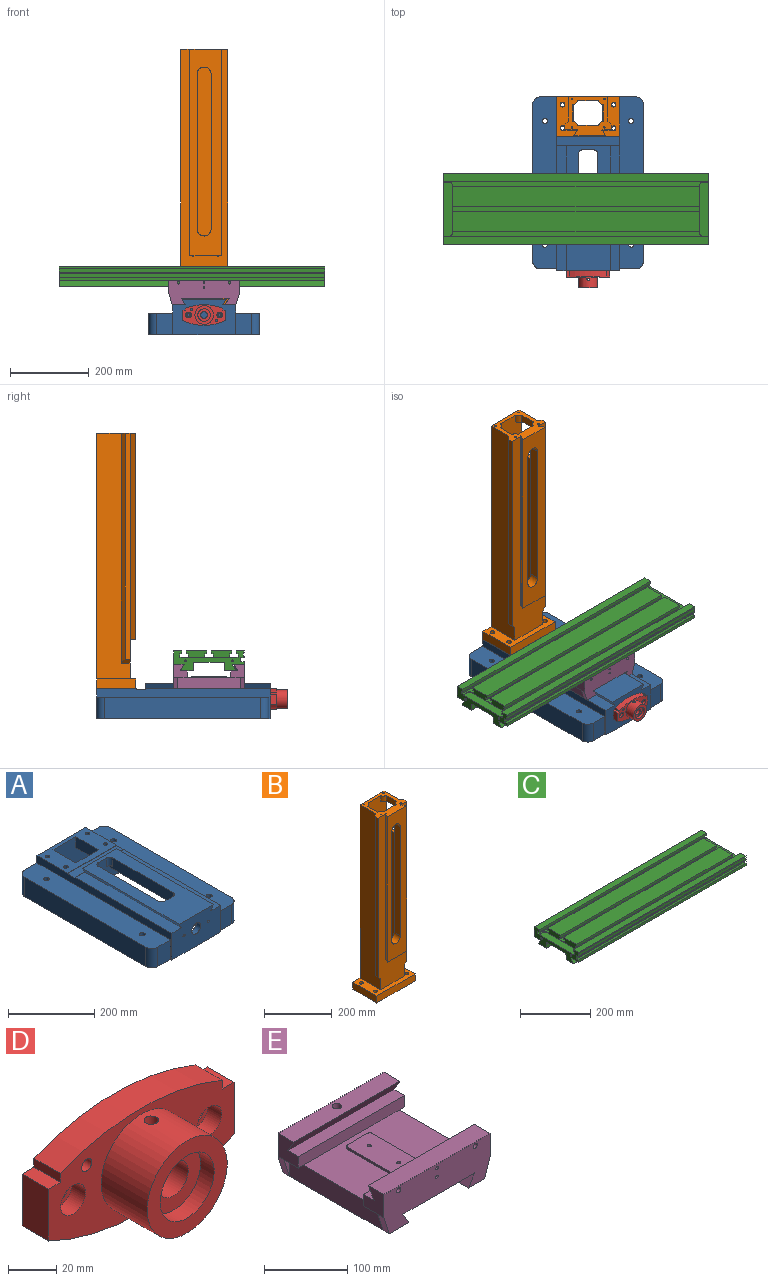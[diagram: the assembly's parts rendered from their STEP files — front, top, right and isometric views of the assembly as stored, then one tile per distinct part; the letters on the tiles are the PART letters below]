
ASSEMBLY  parts=5 mates=4
PART A: 110 faces, bbox 282x443x90 mm
  f0: plane 83x51mm, normal (0,0,-1), area 4078.8mm2, adj f11,f45,f46,f62,f81,f106
  f1: plane 100x36mm, normal (0,0,-1), area 3600mm2, adj f2,f77,f91,f102
  f2: plane 293x26mm, normal (-1,0,0), area 7222.3mm2, adj f1,f7,f10,f11,f13,f82,f89,f90
  f3: plane 83x36mm, normal (0,0,-1), area 2988mm2, adj f4,f11,f75,f100
  f4: plane 293x26mm, normal (1,0,0), area 7222.3mm2, adj f3,f8,f10,f11,f70,f80,f86,f87
  f5: plane 100x51mm, normal (0,0,-1), area 5100mm2, adj f50,f79,f85,f96
  f6: plane 100x51mm, normal (0,0,-1), area 5100mm2, adj f46,f81,f94,f105
  f7: plane 90x36mm, normal (0,0,-1), area 3240mm2, adj f2,f10,f77,f90
  f8: plane 100x36mm, normal (0,0,-1), area 3600mm2, adj f4,f75,f88,f99
  f9: plane 90x51mm, normal (0,0,-1), area 4590mm2, adj f10,f50,f79,f84
  f10: plane 262x90mm, normal (0,-1,0), area 9651.3mm2, adj f2,f4,f7,f9,f15,f16,f19,f20
  f11: plane 242x65mm, normal (0,1,0), area 12693.9mm2, adj f0,f2,f3,f4,f12,f13,f14,f21
  f12: plane 83x51mm, normal (0,0,-1), area 4078.8mm2, adj f11,f50,f51,f67,f79,f97
  f13: plane 83x36mm, normal (0,0,-1), area 2988mm2, adj f2,f11,f77,f103
  f14: plane 84x48mm, normal (0,0,-1), area 3594.9mm2, adj f11,f21,f22,f23,f24,f25
  f15: plane 10x10mm, normal (0,0,-1), area 21.5mm2, adj f10,f19,f25
  f16: plane 10x10mm, normal (0,0,-1), area 21.5mm2, adj f10,f20,f21
  f17: plane 108x93.5mm, normal (0,0,-1), area 9780.4mm2, adj f27,f28,f47,f48,f63,f64,f68,f73
  f18: plane 108x93.5mm, normal (0,0,-1), area 9780.4mm2, adj f27,f29,f48,f49,f61,f65,f66,f72
  f19: cylinder r=10mm len=25mm, axis (0,0,1), area 392.7mm2, adj f10,f15,f25,f55
  f20: cylinder r=10mm len=25mm, axis (0,0,1), area 392.7mm2, adj f10,f16,f21,f55
  f21: plane 293x31mm, normal (1,0,0), area 6733mm2, adj f10,f11,f14,f16,f20,f22,f55,f76
  f22: cylinder r=10mm len=25mm, axis (0,0,1), area 392.7mm2, adj f14,f21,f23,f55
  f23: plane 28x25mm, normal (0,1,0), area 700mm2, adj f14,f22,f24,f55
  f24: cylinder r=10mm len=25mm, axis (0,0,1), area 392.7mm2, adj f14,f23,f25,f55
  f25: plane 293x31mm, normal (-1,0,0), area 6733mm2, adj f10,f11,f14,f15,f19,f24,f55,f78
  f26: plane 443x282mm, normal (0,0,-1), area 14950.5mm2, adj f10,f11,f27,f28,f29,f33,f34,f36
  f27: plane 262x62mm, normal (0,1,0), area 7666.3mm2, adj f17,f18,f26,f28,f29,f69,f72,f73
  f28: plane 98x45mm, normal (-1,0,0), area 4410mm2, adj f17,f26,f27,f47
  f29: plane 98x45mm, normal (1,0,0), area 4410mm2, adj f18,f26,f27,f49
  f30: plane 160x101mm, normal (0,0,1), area 10208.1mm2, adj f33,f40,f48,f52,f59,f61,f64,f65
  f31: plane 90x51mm, normal (0,0,-1), area 4590mm2, adj f10,f46,f81,f93
  f32: plane 318x32.08mm, normal (0,0,1), area 10202.4mm2, adj f33,f54,f57,f58
  f33: plane 443x76mm, normal (-1,0,0), area 9554mm2, adj f26,f30,f32,f36,f40,f44,f57,f58
  f34: plane 55x41mm, normal (0,-1,0), area 2255mm2, adj f26,f35,f37,f52
  f35: plane 438x61mm, normal (0,0,1), area 26280.9mm2, adj f34,f37,f38,f39,f40,f52,f62,f63
  f36: plane 55x41mm, normal (0,-1,0), area 2255mm2, adj f26,f33,f43,f44
  f37: cylinder r=20mm len=55mm, axis (0,0,1), area 1727.9mm2, adj f26,f34,f35,f38
  f38: plane 398x55mm, normal (1,0,0), area 21890mm2, adj f26,f35,f37,f39
  f39: cylinder r=20mm len=55mm, axis (0,0,1), area 1727.9mm2, adj f26,f35,f38,f40
  f40: plane 242x76mm, normal (0,1,0), area 16670mm2, adj f26,f30,f33,f35,f39,f41,f44,f52
  f41: cylinder r=20mm len=55mm, axis (0,0,1), area 1727.9mm2, adj f26,f40,f42,f44
  f42: plane 398x55mm, normal (-1,0,0), area 21890mm2, adj f26,f41,f43,f44
  f43: cylinder r=20mm len=55mm, axis (0,0,1), area 1727.9mm2, adj f26,f36,f42,f44
  f44: plane 438x61mm, normal (0,0,1), area 26280.9mm2, adj f33,f36,f40,f41,f42,f43,f66,f67
  f45: cylinder r=10mm len=45mm, axis (0,0,1), area 706.9mm2, adj f0,f11,f26,f46
  f46: plane 283x45mm, normal (-1,0,0), area 12184.1mm2, adj f0,f6,f10,f26,f31,f45,f92,f93
  f47: cylinder r=10mm len=45mm, axis (0,0,1), area 706.9mm2, adj f17,f26,f28,f48
  f48: plane 242x76mm, normal (0,-1,0), area 13215mm2, adj f17,f18,f26,f30,f47,f49,f72,f73
  f49: cylinder r=10mm len=45mm, axis (0,0,1), area 706.9mm2, adj f18,f26,f29,f48
  f50: plane 283x45mm, normal (1,0,0), area 12184.1mm2, adj f5,f9,f10,f12,f26,f51,f83,f84
  f51: cylinder r=10mm len=45mm, axis (0,0,1), area 706.9mm2, adj f11,f12,f26,f50
  f52: plane 443x76mm, normal (1,0,0), area 9554mm2, adj f26,f30,f34,f35,f40,f53,f57,f58
  f53: plane 318x32.08mm, normal (0,0,1), area 10202.4mm2, adj f52,f56,f57,f58
  f54: plane 318x14mm, normal (-0.87,0,-0.5), area 5140.7mm2, adj f32,f55,f57,f58
  f55: plane 318x112mm, normal (0,0,1), area 25189.8mm2, adj f10,f19,f20,f21,f22,f23,f24,f25
  f56: plane 318x14mm, normal (0.87,0,-0.5), area 5140.7mm2, adj f53,f55,f57,f58
  f57: plane 160x90mm, normal (0,-1,0), area 12858.7mm2, adj f26,f32,f33,f52,f53,f54,f55,f56
  f58: plane 160x15mm, normal (0,1,0), area 1614.8mm2, adj f32,f33,f52,f53,f54,f55,f56,f60
  f59: plane 160x1mm, normal (0,-1,0), area 160mm2, adj f30,f33,f52,f60
  f60: plane 160x24mm, normal (0,0,1), area 3840mm2, adj f33,f52,f58,f59
  f61: cylinder r=5.1mm len=31mm, axis (0,0,1), area 993.4mm2, adj f18,f30
  f62: cylinder r=6.5mm len=13mm, axis (0,0,1), area 408.4mm2, adj f0,f35
  f63: cylinder r=6.5mm len=13mm, axis (0,0,1), area 408.4mm2, adj f17,f35
  f64: cylinder r=5.1mm len=31mm, axis (0,0,1), area 993.4mm2, adj f17,f30
  f65: cylinder r=5.1mm len=31mm, axis (0,0,1), area 993.4mm2, adj f18,f30
  f66: cylinder r=6.5mm len=13mm, axis (0,0,1), area 408.4mm2, adj f18,f44
  f67: cylinder r=6.5mm len=13mm, axis (0,0,1), area 408.4mm2, adj f12,f44
  f68: cylinder r=5.1mm len=31mm, axis (0,0,1), area 993.4mm2, adj f17,f30
  f69: cylinder r=228.11mm len=238mm, axis (0,1,0), area 4256.5mm2, adj f10,f26,f27
  f70: plane 90x36mm, normal (0,0,-1), area 3240mm2, adj f4,f10,f75,f87
  f71: plane 75x14mm, normal (0,1,0), area 1050mm2, adj f30,f72,f73,f74
  f72: plane 108x31mm, normal (1,0,0), area 2886mm2, adj f18,f27,f30,f48,f71,f74
  f73: plane 108x31mm, normal (-1,0,0), area 2886mm2, adj f17,f27,f30,f48,f71,f74
  f74: plane 75x33mm, normal (0,0,-1), area 2475mm2, adj f27,f71,f72,f73
  f75: plane 293x6mm, normal (-1,0,0), area 1698mm2, adj f3,f8,f10,f11,f70,f76,f86,f87
  f76: plane 293x10mm, normal (0,0,-1), area 2930mm2, adj f10,f11,f21,f75
  f77: plane 293x6mm, normal (1,0,0), area 1698mm2, adj f1,f7,f10,f11,f13,f78,f89,f90
  f78: plane 293x10mm, normal (0,0,-1), area 2930mm2, adj f10,f11,f25,f77
  f79: plane 293x6mm, normal (-1,0,0), area 1682.7mm2, adj f5,f9,f10,f11,f12,f80,f83,f84
  f80: plane 293x10mm, normal (0,0,-1), area 2930mm2, adj f4,f10,f11,f79
  f81: plane 293x6mm, normal (1,0,0), area 1682.7mm2, adj f0,f6,f10,f11,f31,f82,f92,f93
  f82: plane 293x10mm, normal (0,0,-1), area 2930mm2, adj f2,f10,f11,f81
  f83: plane 51x23.78mm, normal (0.42,0,-0.91), area 562.7mm2, adj f50,f79,f84,f85
  f84: plane 51x27.55mm, normal (0,1,0), area 798.5mm2, adj f9,f50,f79,f83
  f85: plane 51x27.55mm, normal (0,-1,0), area 798.5mm2, adj f5,f50,f79,f83
  f86: plane 36x16.79mm, normal (0.42,0,-0.91), area 397.2mm2, adj f4,f75,f87,f88
  f87: plane 36x19.79mm, normal (0,1,0), area 410.2mm2, adj f4,f70,f75,f86
  f88: plane 36x19.79mm, normal (0,-1,0), area 410.2mm2, adj f4,f8,f75,f86
  f89: plane 36x16.79mm, normal (-0.42,0,-0.91), area 397.2mm2, adj f2,f77,f90,f91
  f90: plane 36x19.79mm, normal (0,1,0), area 410.2mm2, adj f2,f7,f77,f89
  f91: plane 36x19.79mm, normal (0,-1,0), area 410.2mm2, adj f1,f2,f77,f89
  f92: plane 51x23.78mm, normal (-0.42,0,-0.91), area 562.7mm2, adj f46,f81,f93,f94
  f93: plane 51x27.55mm, normal (0,1,0), area 798.5mm2, adj f31,f46,f81,f92
  f94: plane 51x27.55mm, normal (0,-1,0), area 798.5mm2, adj f6,f46,f81,f92
  f95: plane 51x23.78mm, normal (0.42,0,-0.91), area 562.7mm2, adj f50,f79,f96,f97
  f96: plane 51x27.55mm, normal (0,1,0), area 798.5mm2, adj f5,f50,f79,f95
  f97: plane 51x27.55mm, normal (0,-1,0), area 798.5mm2, adj f12,f50,f79,f95
  f98: plane 36x16.79mm, normal (0.42,0,-0.91), area 397.2mm2, adj f4,f75,f99,f100
  f99: plane 36x19.79mm, normal (0,1,0), area 410.2mm2, adj f4,f8,f75,f98
  f100: plane 36x19.79mm, normal (0,-1,0), area 410.2mm2, adj f3,f4,f75,f98
  f101: plane 36x16.79mm, normal (-0.42,0,-0.91), area 397.2mm2, adj f2,f77,f102,f103
  f102: plane 36x19.79mm, normal (0,1,0), area 410.2mm2, adj f1,f2,f77,f101
  f103: plane 36x19.79mm, normal (0,-1,0), area 410.2mm2, adj f2,f13,f77,f101
  f104: plane 51x23.78mm, normal (-0.42,0,-0.91), area 562.7mm2, adj f46,f81,f105,f106
  f105: plane 51x27.55mm, normal (0,1,0), area 798.5mm2, adj f6,f46,f81,f104
  f106: plane 51x27.55mm, normal (0,-1,0), area 798.5mm2, adj f0,f46,f81,f104
  f107: cylinder r=14.75mm len=29.5mm, axis (0,1,0), area 1390.2mm2, adj f11,f57
  f108: cylinder r=3.4mm len=15mm, axis (0,-1,0), area 320.4mm2, adj f11,f57
  f109: cylinder r=3.4mm len=15mm, axis (0,-1,0), area 320.4mm2, adj f11,f57
PART B: 65 faces, bbox 160x100x650 mm
  f0: plane 625x120mm, normal (0,-1,0), area 38554.6mm2, adj f2,f3,f7,f8,f13,f18,f27,f33
  f1: plane 525x12.84mm, normal (0.87,0.5,0), area 7780.8mm2, adj f2,f3,f15,f61
  f2: plane 120x100mm, normal (0,0,1), area 5239.5mm2, adj f0,f1,f6,f7,f8,f9,f10,f11
  f3: plane 80x15mm, normal (0,0,-1), area 1067.4mm2, adj f0,f1,f15,f16,f57,f59,f60,f61
  f4: plane 5x5mm, normal (-1,0,0), area 5.4mm2, adj f11,f48,f56
  f5: plane 535x64mm, normal (-1,0,0), area 33925.4mm2, adj f10,f11,f26,f54,f55
  f6: plane 20x10mm, normal (0.71,0.71,0), area 282.8mm2, adj f2,f7,f8,f48
  f7: plane 575x12mm, normal (1,0,0), area 6210.7mm2, adj f0,f2,f6,f14,f33,f48,f51,f52
  f8: plane 625x85mm, normal (1,0,0), area 34965.7mm2, adj f0,f2,f6,f11,f14,f18,f20,f33
  f9: plane 42.27x20mm, normal (-1,0,0), area 845.4mm2, adj f2,f47,f48,f49
  f10: plane 650x78mm, normal (0,1,0), area 35005.8mm2, adj f2,f5,f12,f26,f29,f30,f31,f32
  f11: plane 650x89mm, normal (0,-1,0), area 51186.6mm2, adj f2,f4,f5,f8,f12,f26,f45,f46
  f12: plane 650x64mm, normal (1,0,0), area 41165.4mm2, adj f2,f10,f11,f26,f43,f44,f45,f46
  f13: plane 575x12mm, normal (-1,0,0), area 6900mm2, adj f0,f2,f28,f34
  f14: plane 465x10mm, normal (0.71,0.71,0), area 6505.4mm2, adj f7,f8,f33,f54
  f15: plane 525x80mm, normal (0,-1,0), area 26798.1mm2, adj f1,f2,f3,f16,f29,f30,f31,f32
  f16: plane 525x12.84mm, normal (-0.87,0.5,0), area 7780.8mm2, adj f2,f3,f15,f59
  f17: plane 160x25mm, normal (0,-1,0), area 4000mm2, adj f18,f19,f21,f26
  f18: plane 160x100mm, normal (0,0,1), area 7047.6mm2, adj f0,f8,f17,f19,f20,f21,f22,f23
  f19: plane 100x25mm, normal (1,0,0), area 2500mm2, adj f17,f18,f20,f26
  f20: plane 650x160mm, normal (0,1,0), area 66500mm2, adj f2,f8,f18,f19,f21,f26,f27
  f21: plane 100x25mm, normal (-1,0,0), area 2500mm2, adj f17,f18,f20,f26
  f22: cylinder r=6mm len=25mm, axis (0,0,-1), area 942.5mm2, adj f18,f26
  f23: cylinder r=6mm len=25mm, axis (0,0,-1), area 942.5mm2, adj f18,f26
  f24: cylinder r=6mm len=25mm, axis (0,0,-1), area 942.5mm2, adj f18,f26
  f25: cylinder r=6mm len=25mm, axis (0,0,-1), area 942.5mm2, adj f18,f26
  f26: plane 160x100mm, normal (0,0,-1), area 10555.6mm2, adj f5,f10,f11,f12,f17,f19,f20,f21
  f27: plane 625x85mm, normal (-1,0,0), area 40255mm2, adj f0,f2,f18,f20,f28,f34
  f28: plane 585x10mm, normal (-0.71,0.71,0), area 8202.4mm2, adj f2,f13,f27,f34
  f29: cylinder r=18mm len=36mm, axis (0,-1,0), area 1470.3mm2, adj f10,f15,f30,f31
  f30: plane 394x26mm, normal (1,0,0), area 10244mm2, adj f10,f15,f29,f32
  f31: plane 394x26mm, normal (-1,0,0), area 10244mm2, adj f10,f15,f29,f32
  f32: cylinder r=18mm len=36mm, axis (0,-1,0), area 1470.3mm2, adj f10,f15,f30,f31
  f33: plane 22x10mm, normal (0.71,0,-0.71), area 240.4mm2, adj f0,f7,f8,f14
  f34: plane 22x10mm, normal (-0.71,0,-0.71), area 240.4mm2, adj f0,f13,f27,f28
  f35: cylinder r=2.1mm len=10.4mm, axis (0,0,1), area 137.2mm2, adj f2,f36
  f36: cone r=0mm half-angle=59deg, axis (0,0,1), area 16.2mm2, adj f35
  f37: cylinder r=2.1mm len=10.4mm, axis (0,0,1), area 137.2mm2, adj f2,f38
  f38: cone r=0mm half-angle=59deg, axis (0,0,1), area 16.2mm2, adj f37
  f39: cylinder r=2.1mm len=10.4mm, axis (0,0,1), area 137.2mm2, adj f2,f40
  f40: cone r=0mm half-angle=59deg, axis (0,0,1), area 16.2mm2, adj f39
  f41: cylinder r=2.1mm len=10.4mm, axis (0,0,1), area 137.2mm2, adj f2,f42
  f42: cone r=0mm half-angle=59deg, axis (0,0,1), area 16.2mm2, adj f41
  f43: cylinder r=15mm len=20mm, axis (0,0,1), area 339.7mm2, adj f2,f10,f12,f44
  f44: plane 12.31x10.37mm, normal (0,0,-1), area 89.3mm2, adj f10,f12,f43
  f45: cylinder r=15mm len=20mm, axis (0,0,1), area 360.5mm2, adj f2,f11,f12,f46
  f46: plane 12.59x11.37mm, normal (0,0,-1), area 101.8mm2, adj f11,f12,f45
  f47: cylinder r=15mm len=20mm, axis (0,0,1), area 360.5mm2, adj f2,f9,f11,f48
  f48: plane 65x33.59mm, normal (0,0,-1), area 921.1mm2, adj f4,f6,f7,f8,f9,f10,f11,f47
  f49: cylinder r=15mm len=20mm, axis (0,0,1), area 339.7mm2, adj f2,f9,f10,f48
  f50: plane 100x6mm, normal (1,0,0), area 589.3mm2, adj f10,f48,f51,f52,f53,f54
  f51: cylinder r=5mm len=21mm, axis (1,0,0), area 164.9mm2, adj f7,f48,f50,f52
  f52: plane 90x21mm, normal (0,1,0), area 1890mm2, adj f7,f50,f51,f53
  f53: cylinder r=5mm len=21mm, axis (1,0,0), area 164.9mm2, adj f7,f50,f52,f54
  f54: plane 60x21mm, normal (0,0,1), area 730mm2, adj f5,f7,f8,f14,f50,f53,f55
  f55: cylinder r=5mm len=11mm, axis (1,0,0), area 86.4mm2, adj f5,f8,f11,f54
  f56: cylinder r=5mm len=11mm, axis (1,0,0), area 86.4mm2, adj f4,f8,f11,f48
  f57: plane 528x2.17mm, normal (-0.87,-0.5,0), area 1315.9mm2, adj f0,f2,f3,f58,f59,f63
  f58: plane 526.75x1.88mm, normal (0.5,-0.87,0), area 1140.4mm2, adj f0,f2,f57,f63
  f59: plane 525x1.88mm, normal (-0.5,0.87,0), area 1136.7mm2, adj f2,f3,f16,f57
  f60: plane 528x2.17mm, normal (0.87,-0.5,0), area 1315.9mm2, adj f0,f2,f3,f61,f62,f64
  f61: plane 525x1.88mm, normal (0.5,0.87,0), area 1136.7mm2, adj f1,f2,f3,f60
  f62: plane 526.75x1.88mm, normal (-0.5,-0.87,0), area 1140.4mm2, adj f0,f2,f60,f64
  f63: cylinder r=1.25mm len=2.5mm, axis (-0.87,-0.5,0), area 2.7mm2, adj f0,f57,f58
  f64: cylinder r=1.25mm len=2.5mm, axis (-0.87,0.5,0), area 2.7mm2, adj f0,f60,f62
PART C: 68 faces, bbox 675x180x50 mm
  f0: plane 628x51.5mm, normal (0,0,1), area 32342mm2, adj f5,f6,f50,f55
  f1: plane 628x51.5mm, normal (0,0,1), area 32342mm2, adj f12,f13,f50,f55
  f2: plane 675x20.75mm, normal (0,0,1), area 13303mm2, adj f3,f17,f18,f43,f48,f50,f52,f54
  f3: plane 628x8.5mm, normal (0,1,0), area 5338mm2, adj f2,f4,f50,f55
  f4: plane 628x4.38mm, normal (0,0,-1), area 2747.5mm2, adj f3,f5,f50,f55
  f5: plane 628x7.5mm, normal (0,1,0), area 4710mm2, adj f0,f4,f50,f55
  f6: plane 628x7.5mm, normal (0,-1,0), area 4710mm2, adj f0,f7,f50,f55
  f7: plane 628x4.38mm, normal (0,0,-1), area 2747.5mm2, adj f6,f8,f50,f55
  f8: plane 628x8.5mm, normal (0,-1,0), area 5338mm2, adj f7,f9,f50,f55
  f9: plane 628x20.75mm, normal (0,0,1), area 13031mm2, adj f8,f10,f50,f55
  f10: plane 628x8.5mm, normal (0,1,0), area 5338mm2, adj f9,f11,f50,f55
  f11: plane 628x4.38mm, normal (0,0,-1), area 2747.5mm2, adj f10,f12,f50,f55
  f12: plane 628x7.5mm, normal (0,1,0), area 4710mm2, adj f1,f11,f50,f55
  f13: plane 628x7.5mm, normal (0,-1,0), area 4710mm2, adj f1,f14,f50,f55
  f14: plane 628x4.38mm, normal (0,0,-1), area 2747.5mm2, adj f13,f15,f50,f55
  f15: plane 628x8.5mm, normal (0,-1,0), area 5338mm2, adj f14,f16,f50,f55
  f16: plane 675x20.75mm, normal (0,0,1), area 13303mm2, adj f15,f17,f18,f44,f49,f50,f51,f55
  f17: plane 180x50mm, normal (1,0,0), area 3867.8mm2, adj f2,f16,f19,f20,f21,f22,f23,f24
  f18: plane 180x50mm, normal (-1,0,0), area 3867.8mm2, adj f2,f16,f19,f20,f21,f22,f23,f24
  f19: plane 675x4mm, normal (0,-1,0), area 2700mm2, adj f17,f18,f20,f47
  f20: plane 675x2.5mm, normal (0,0,-1), area 1687.5mm2, adj f17,f18,f19,f21
  f21: plane 675x10mm, normal (0,-1,0), area 6750mm2, adj f17,f18,f20,f22
  f22: plane 675x2.5mm, normal (0,0,1), area 1687.5mm2, adj f17,f18,f21,f23
  f23: plane 675x3.7mm, normal (0,-1,0), area 2497.5mm2, adj f17,f18,f22,f24
  f24: plane 675x10mm, normal (0,0.18,-0.98), area 6864.5mm2, adj f17,f18,f23,f25
  f25: plane 675x12mm, normal (0,-1,0), area 8100mm2, adj f17,f18,f24,f26
  f26: plane 675x10mm, normal (0,0.18,0.98), area 6864.5mm2, adj f17,f18,f25,f27
  f27: plane 675x8mm, normal (0,-1,0), area 5400mm2, adj f17,f18,f26,f28
  f28: plane 675x30.75mm, normal (0,0,-1), area 20756.3mm2, adj f17,f18,f27,f29
  f29: plane 675x16mm, normal (0,-0.87,0.5), area 12470.8mm2, adj f17,f18,f28,f30
  f30: plane 675x28.49mm, normal (0,0,-1), area 19229.1mm2, adj f17,f18,f29,f31
  f31: plane 675x16.73mm, normal (0,1,-0.05), area 11306.5mm2, adj f17,f18,f30,f32
  f32: cylinder r=5mm len=675mm, axis (-1,0,0), area 5144.6mm2, adj f17,f18,f31,f33
  f33: plane 675x68.45mm, normal (0,0,-1), area 46206.7mm2, adj f17,f18,f32,f34
  f34: cylinder r=5mm len=675mm, axis (-1,0,0), area 5144.6mm2, adj f17,f18,f33,f35
  f35: plane 675x16.73mm, normal (0,-1,-0.05), area 11306.5mm2, adj f17,f18,f34,f36
  f36: plane 675x32.49mm, normal (0,0,-1), area 21929.1mm2, adj f17,f18,f35,f37
  f37: plane 675x16mm, normal (0,0.87,0.5), area 12470.8mm2, adj f17,f18,f36,f38
  f38: plane 675x26.75mm, normal (0,0,-1), area 18056.2mm2, adj f17,f18,f37,f39
  f39: plane 675x34mm, normal (0,1,0), area 22950mm2, adj f17,f18,f38,f40
  f40: plane 675x20.5mm, normal (0,0,1), area 13837.5mm2, adj f17,f18,f39,f41
  f41: plane 675x7.5mm, normal (0,-1,0), area 5062.5mm2, adj f17,f18,f40,f42
  f42: plane 675x4.38mm, normal (0,0,-1), area 2953.1mm2, adj f17,f18,f41,f43
  f43: plane 675x8.5mm, normal (0,-1,0), area 5737.5mm2, adj f2,f17,f18,f42
  f44: plane 675x8.5mm, normal (0,1,0), area 5737.5mm2, adj f16,f17,f18,f45
  f45: plane 675x4.38mm, normal (0,0,-1), area 2953.1mm2, adj f17,f18,f44,f46
  f46: plane 675x7.5mm, normal (0,1,0), area 5062.5mm2, adj f17,f18,f45,f47
  f47: plane 675x20.5mm, normal (0,0,1), area 13837.5mm2, adj f17,f18,f19,f46
  f48: cylinder r=10mm len=10mm, axis (0,0,1), area 23.6mm2, adj f2,f50,f52,f53
  f49: cylinder r=10mm len=10mm, axis (0,0,1), area 23.6mm2, adj f16,f50,f51,f53
  f50: plane 118x17.5mm, normal (-1,0,0), area 1676.2mm2, adj f0,f1,f2,f3,f4,f5,f6,f7
  f51: plane 13.5x1.5mm, normal (0,1,0), area 20.3mm2, adj f16,f18,f49,f53
  f52: plane 13.5x1.5mm, normal (0,-1,0), area 20.3mm2, adj f2,f18,f48,f53
  f53: plane 138x23.5mm, normal (0,0,1), area 3200.1mm2, adj f18,f48,f49,f50,f51,f52
  f54: cylinder r=10mm len=10mm, axis (0,0,1), area 23.6mm2, adj f2,f55,f58,f59
  f55: plane 118x17.5mm, normal (1,0,0), area 1676.2mm2, adj f0,f1,f2,f3,f4,f5,f6,f7
  f56: cylinder r=10mm len=10mm, axis (0,0,1), area 23.6mm2, adj f16,f55,f57,f59
  f57: plane 13.5x1.5mm, normal (0,1,0), area 20.3mm2, adj f16,f17,f56,f59
  f58: plane 13.5x1.5mm, normal (0,-1,0), area 20.3mm2, adj f2,f17,f54,f59
  f59: plane 138x23.5mm, normal (0,0,1), area 3200.1mm2, adj f17,f54,f55,f56,f57,f58
  f60: cylinder r=2.5mm len=21mm, axis (1,0,0), area 329.9mm2, adj f17,f61
  f61: cone r=0mm half-angle=59deg, axis (1,0,0), area 22.9mm2, adj f60
  f62: cylinder r=2.5mm len=21mm, axis (1,0,0), area 329.9mm2, adj f17,f63
  f63: cone r=0mm half-angle=59deg, axis (1,0,0), area 22.9mm2, adj f62
  f64: cylinder r=2.5mm len=21mm, axis (-1,0,0), area 329.9mm2, adj f18,f65
  f65: cone r=0mm half-angle=59deg, axis (-1,0,0), area 22.9mm2, adj f64
  f66: cylinder r=2.5mm len=21mm, axis (-1,0,0), area 329.9mm2, adj f18,f67
  f67: cone r=0mm half-angle=59deg, axis (-1,0,0), area 22.9mm2, adj f66
PART D: 27 faces, bbox 109x42.5x53 mm
  f0: cylinder r=8.6mm len=24.5mm, axis (0,1,0), area 1266.5mm2, adj f20,f22,f23,f24
  f1: cylinder r=23.5mm len=47mm, axis (0,1,0), area 3929.8mm2, adj f12,f18,f23,f24
  f2: cylinder r=4.75mm len=9.5mm, axis (0,1,0), area 223.8mm2, adj f13,f17
  f3: cylinder r=4.75mm len=9.5mm, axis (0,1,0), area 223.8mm2, adj f13,f15
  f4: cylinder r=123.5mm len=109mm, axis (0,1,0), area 1749.8mm2, adj f5,f11,f12,f13
  f5: plane 26.32x15.5mm, normal (1,0,0), area 408mm2, adj f4,f6,f12,f13
  f6: plane 15.5x7mm, normal (0,0,1), area 108.5mm2, adj f5,f7,f12,f13
  f7: plane 15.5x4.5mm, normal (1,0,0), area 69.7mm2, adj f6,f8,f12,f13
  f8: cylinder r=123.5mm len=95mm, axis (0,1,0), area 1511.5mm2, adj f7,f9,f12,f13
  f9: plane 15.5x4.5mm, normal (-1,0,0), area 69.7mm2, adj f8,f10,f12,f13
  f10: plane 15.5x7mm, normal (0,0,1), area 108.5mm2, adj f9,f11,f12,f13
  f11: plane 26.32x15.5mm, normal (-1,0,0), area 408mm2, adj f4,f10,f12,f13
  f12: plane 109x53mm, normal (0,-1,0), area 2712.5mm2, adj f1,f4,f5,f6,f7,f8,f9,f10
  f13: plane 109x53mm, normal (0,1,0), area 3844.2mm2, adj f2,f3,f4,f5,f6,f7,f8,f9
  f14: cylinder r=7.25mm len=14.5mm, axis (0,-1,0), area 364.4mm2, adj f12,f15
  f15: plane 14.5x14.5mm, normal (0,-1,0), area 94.2mm2, adj f3,f14
  f16: cylinder r=7.25mm len=14.5mm, axis (0,-1,0), area 364.4mm2, adj f12,f17
  f17: plane 14.5x14.5mm, normal (0,-1,0), area 94.2mm2, adj f2,f16
  f18: plane 47x47mm, normal (0,-1,0), area 943.2mm2, adj f1,f19
  f19: cylinder r=15.88mm len=31.75mm, axis (0,-1,0), area 798mm2, adj f18,f20
  f20: plane 31.75x31.75mm, normal (0,-1,0), area 559.4mm2, adj f0,f19
  f21: cylinder r=15.88mm len=31.75mm, axis (0,1,0), area 997.5mm2, adj f13,f22
  f22: plane 31.75x31.75mm, normal (0,1,0), area 559.4mm2, adj f0,f21
  f23: cylinder r=3mm len=15.44mm, axis (0,0,-1), area 284.1mm2, adj f0,f1
  f24: cylinder r=3mm len=15.44mm, axis (0,0,-1), area 284.1mm2, adj f0,f1
  f25: cylinder r=3mm len=15.5mm, axis (0,-1,0), area 292.2mm2, adj f12,f13
  f26: cylinder r=3mm len=15.5mm, axis (0,-1,0), area 292.2mm2, adj f12,f13
PART E: 75 faces, bbox 180.8x180.8x63.1 mm
  f0: plane 180x121.47mm, normal (0,0,-1), area 7541.7mm2, adj f11,f12,f19,f20,f60,f62,f63,f64
  f1: cylinder r=2.5mm len=11.8mm, axis (0,0,1), area 185.4mm2, adj f45,f74
  f2: cylinder r=2.5mm len=11.8mm, axis (0,0,1), area 185.4mm2, adj f45,f74
  f3: cylinder r=3.25mm len=32.6mm, axis (0,0,1), area 665.7mm2, adj f58,f61
  f4: plane 162x111mm, normal (0,0,1), area 14223.5mm2, adj f24,f25,f28,f33,f37,f38,f39,f40
  f5: plane 28.3x10.5mm, normal (0.95,0,-0.3), area 311.8mm2, adj f8,f13,f19,f34
  f6: plane 28.3x10.5mm, normal (-0.95,0,-0.3), area 311.8mm2, adj f10,f18,f20,f29
  f7: plane 180x26.75mm, normal (0,0,1), area 4815mm2, adj f8,f16,f19,f26
  f8: plane 34.5x34mm, normal (1,0,0), area 957.8mm2, adj f5,f7,f19,f23,f25,f26,f35
  f9: plane 34.5x34mm, normal (1,0,0), area 957.8mm2, adj f14,f15,f20,f21,f22,f24,f32
  f10: plane 34.5x34mm, normal (-1,0,0), area 957.8mm2, adj f6,f15,f20,f21,f22,f24,f30
  f11: plane 180x17.2mm, normal (0.87,0,0.5), area 3575mm2, adj f0,f18,f19,f20
  f12: plane 180.83x18.03mm, normal (-0.87,0,0.5), area 3491.1mm2, adj f0,f13,f19,f20,f52,f53
  f13: plane 180x27.31mm, normal (0,0,-1), area 4915.7mm2, adj f5,f12,f14,f19,f20,f33
  f14: plane 28.3x10.5mm, normal (0.95,0,-0.3), area 311.8mm2, adj f9,f13,f20,f36
  f15: plane 180x26.75mm, normal (0,0,1), area 4720mm2, adj f9,f10,f20,f21,f59
  f16: plane 34.5x34mm, normal (-1,0,0), area 957.8mm2, adj f7,f17,f19,f23,f25,f26,f27
  f17: plane 28.3x10.5mm, normal (-0.95,0,-0.3), area 311.8mm2, adj f16,f18,f19,f31
  f18: plane 180x33.08mm, normal (0,0,-1), area 5954.9mm2, adj f6,f11,f17,f19,f20,f28
  f19: plane 180x62.3mm, normal (0,-1,0), area 8940.5mm2, adj f0,f5,f7,f8,f11,f12,f13,f16
  f20: plane 180x62.3mm, normal (0,1,0), area 9013.1mm2, adj f0,f6,f9,f10,f11,f12,f13,f14
  f21: plane 180x17mm, normal (0,-0.87,-0.5), area 3533.4mm2, adj f9,f10,f15,f22
  f22: plane 180x17.57mm, normal (0,0,1), area 3161.7mm2, adj f9,f10,f21,f24
  f23: plane 180x17.57mm, normal (0,0,1), area 3161.7mm2, adj f8,f16,f25,f26
  f24: plane 180x17mm, normal (0,-1,0), area 3060mm2, adj f4,f9,f10,f22,f30,f32
  f25: plane 180x17mm, normal (0,1,0), area 3060mm2, adj f4,f8,f16,f23,f27,f35
  f26: plane 180x17mm, normal (0,0.87,-0.5), area 3449.5mm2, adj f7,f8,f16,f23,f46,f47
  f27: plane 24x9mm, normal (0,0,-1), area 216mm2, adj f16,f25,f28,f31
  f28: plane 159x28.3mm, normal (-1,0,0), area 4499.7mm2, adj f4,f18,f27,f29,f30,f31
  f29: plane 28.3x9mm, normal (0,-1,0), area 127.4mm2, adj f6,f28,f30
  f30: plane 24x9mm, normal (0,0,-1), area 216mm2, adj f10,f24,f28,f29
  f31: plane 28.3x9mm, normal (0,1,0), area 127.4mm2, adj f17,f27,f28
  f32: plane 24x9mm, normal (0,0,-1), area 216mm2, adj f9,f24,f33,f36
  f33: plane 159x28.3mm, normal (1,0,0), area 4427.1mm2, adj f4,f13,f32,f34,f35,f36,f52,f53
  f34: plane 28.3x9mm, normal (0,1,0), area 127.4mm2, adj f5,f33,f35
  f35: plane 24x9mm, normal (0,0,-1), area 216mm2, adj f8,f25,f33,f34
  f36: plane 28.3x9mm, normal (0,-1,0), area 127.3mm2, adj f14,f32,f33
  f37: cylinder r=5mm len=5mm, axis (0,0,-1), area 25.1mm2, adj f4,f38,f44,f45
  f38: plane 32x3.2mm, normal (0,1,0), area 102.4mm2, adj f4,f37,f39,f45
  f39: cylinder r=5mm len=5mm, axis (0,0,-1), area 25.1mm2, adj f4,f38,f40,f45
  f40: plane 80x3.2mm, normal (-1,0,0), area 256mm2, adj f4,f39,f41,f45
  f41: cylinder r=5mm len=5mm, axis (0,0,-1), area 25.1mm2, adj f4,f40,f42,f45
  f42: plane 32x3.2mm, normal (0,-1,0), area 102.4mm2, adj f4,f41,f43,f45
  f43: cylinder r=5mm len=5mm, axis (0,0,-1), area 25.1mm2, adj f4,f42,f44,f45
  f44: plane 80x3.2mm, normal (1,0,0), area 256mm2, adj f4,f37,f43,f45
  f45: plane 90x42mm, normal (0,0,1), area 3719.3mm2, adj f1,f2,f37,f38,f39,f40,f41,f42
  f46: cylinder r=3.4mm len=25.28mm, axis (0,-1,0), area 497.5mm2, adj f19,f26
  f47: cylinder r=3.4mm len=25.28mm, axis (0,-1,0), area 497.5mm2, adj f19,f26
  f48: cylinder r=2.1mm len=13mm, axis (0,-1,0), area 171.5mm2, adj f19,f49
  f49: cone r=0mm half-angle=59deg, axis (0,-1,0), area 16.2mm2, adj f48
  f50: cylinder r=2.1mm len=13mm, axis (0,-1,0), area 171.5mm2, adj f19,f51
  f51: cone r=0mm half-angle=59deg, axis (0,-1,0), area 16.2mm2, adj f50
  f52: cylinder r=3.4mm len=24.65mm, axis (1,0,0), area 484.7mm2, adj f12,f33
  f53: cylinder r=3.4mm len=24.65mm, axis (1,0,0), area 484.7mm2, adj f12,f33
  f54: cylinder r=2.1mm len=12mm, axis (0,1,0), area 158.3mm2, adj f20,f55
  f55: cone r=0mm half-angle=59deg, axis (0,1,0), area 16.2mm2, adj f54
  f56: cylinder r=2.1mm len=12mm, axis (0,1,0), area 158.3mm2, adj f20,f57
  f57: cone r=0mm half-angle=59deg, axis (0,1,0), area 16.2mm2, adj f56
  f58: plane 11x11mm, normal (0,0,1), area 61.9mm2, adj f3,f59
  f59: cylinder r=5.5mm len=11mm, axis (0,0,1), area 276.5mm2, adj f15,f58
  f60: cylinder r=7.5mm len=15mm, axis (0,0,-1), area 212.1mm2, adj f0,f61
  f61: plane 15x15mm, normal (0,0,-1), area 143.5mm2, adj f3,f60
  f62: plane 150x2.5mm, normal (1,0,0), area 375mm2, adj f0,f63,f73,f74
  f63: cylinder r=5mm len=5mm, axis (0,0,-1), area 19.6mm2, adj f0,f62,f64,f74
  f64: plane 23.75x2.5mm, normal (0,-1,0), area 59.4mm2, adj f0,f63,f65,f74
  f65: cylinder r=5mm len=4.78mm, axis (0,0,-1), area 15.9mm2, adj f0,f64,f66,f74
  f66: cylinder r=12mm len=22.94mm, axis (0,0,-1), area 76.3mm2, adj f0,f65,f67,f74
  f67: cylinder r=5mm len=4.78mm, axis (0,0,-1), area 15.9mm2, adj f0,f66,f68,f74
  f68: plane 23.75x2.5mm, normal (0,-1,0), area 59.4mm2, adj f0,f67,f69,f74
  f69: cylinder r=5mm len=5mm, axis (0,0,-1), area 19.6mm2, adj f0,f68,f70,f74
  f70: plane 150x2.5mm, normal (-1,0,0), area 375mm2, adj f0,f69,f71,f74
  f71: cylinder r=5mm len=5mm, axis (0,0,-1), area 19.6mm2, adj f0,f70,f72,f74
  f72: plane 80x2.5mm, normal (0,1,0), area 200mm2, adj f0,f71,f73,f74
  f73: cylinder r=5mm len=5mm, axis (0,0,-1), area 19.6mm2, adj f0,f62,f72,f74
  f74: plane 160x90mm, normal (0,0,-1), area 14106.6mm2, adj f1,f2,f62,f63,f64,f65,f66,f67
PLACE A at identity fixed
PLACE B t=(0,169,21)mm
PLACE C t=(-30.76,-66.95,67.3)mm
PLACE D t=(0,-224,-5)mm
PLACE E t=(0,23.05,21)mm
MATE slider C.f18 <-> E.f10  axis (-1,0,0) through (-368.26,-3.7,83.3)mm
MATE fastened D.f0 <-> A.f107  axis (0,1,0) through (0,-224,-5)mm
MATE fastened B.f24 <-> A.f64  axis (0,0,-1) through (65,199,21)mm
MATE slider E.f19 <-> A.f57  axis (0,-1,0) through (-47.92,-156.95,21)mm
